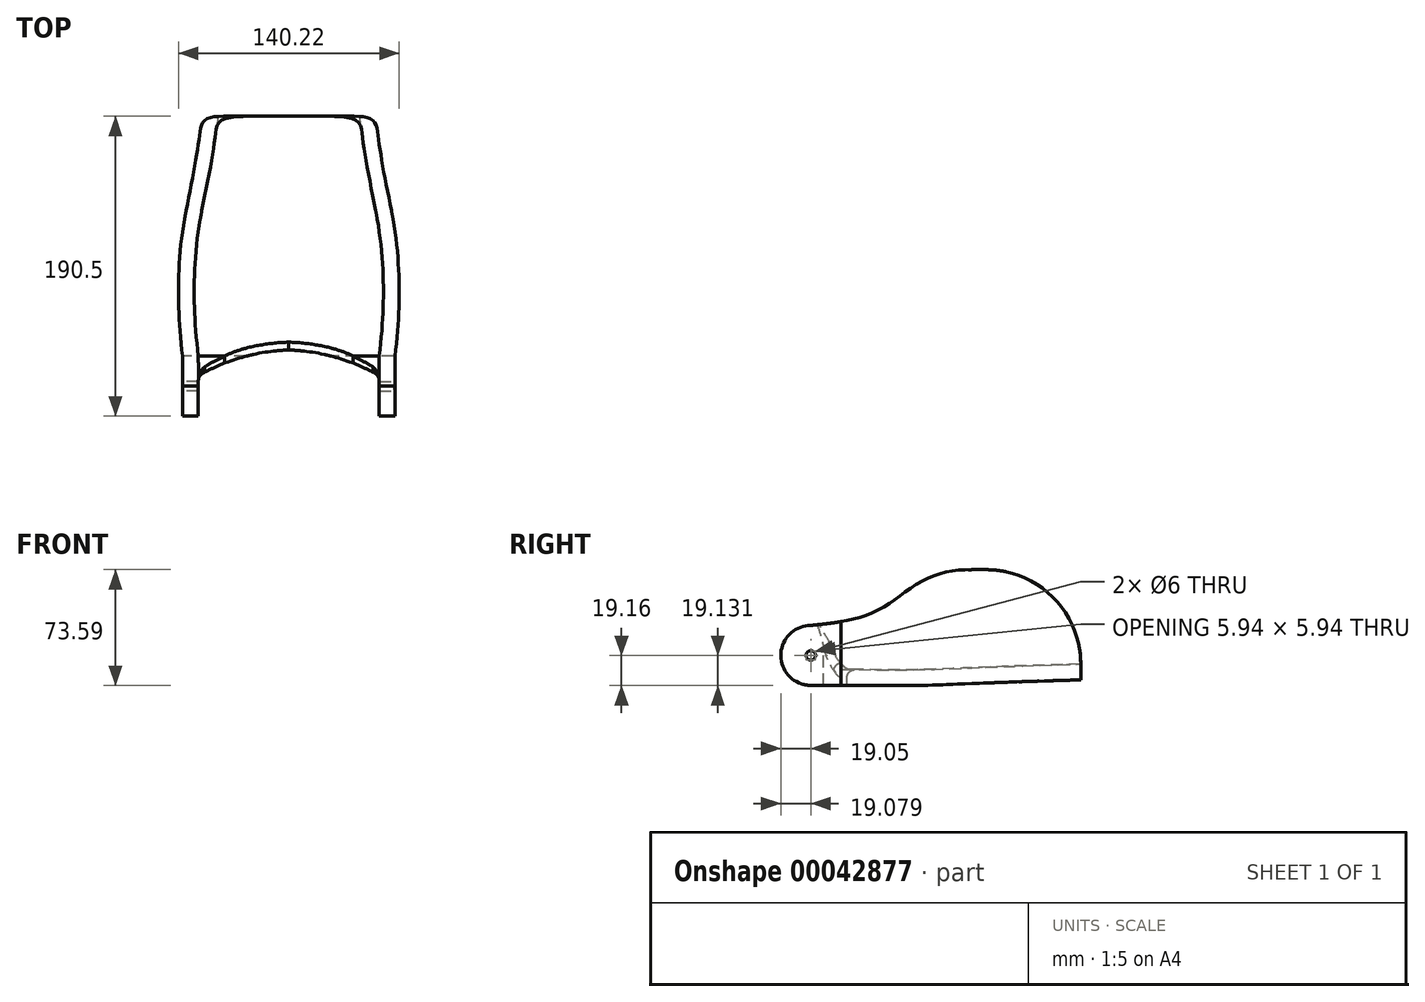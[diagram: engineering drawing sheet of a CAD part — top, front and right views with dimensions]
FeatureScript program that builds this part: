
annotation { "Feature Type Name" : "Feature", "Feature Type Description" : "" }
export const myFeature = defineFeature(function(context is Context, id is Id, definition is map)
    precondition{}
    {
        {
            var Q0;
            Q0=qCreatedBy(makeId("Right.planeOp"),FACE);
            cPlane(context, id + "F0", {"entities" : qUnion([Q0]), "cplaneType" : CPlaneType.OFFSET, "offset" : (115 * mm / 2) + 10 * mm, "width" : 150 * mm, "height" : 150 * mm});
        }
        {
            var Q0;
            Q0=qCreatedBy(makeId("Front.planeOp"),FACE);
            cPlane(context, id + "F1", {"entities" : qUnion([Q0]), "cplaneType" : CPlaneType.OFFSET, "offset" : 114.3 * mm, "width" : 150 * mm, "height" : 150 * mm});
        }
        {
            var Q0;
            Q0=qCreatedBy(makeId("Front.planeOp"),FACE);
            cPlane(context, id + "F2", {"entities" : qUnion([Q0]), "cplaneType" : CPlaneType.OFFSET, "offset" : 76.2 * mm, "width" : 150 * mm, "height" : 150 * mm});
        }
        {
            var Q0;
            Q0=qCreatedBy(makeId("Front.planeOp"),FACE);
            cPlane(context, id + "F3", {"entities" : qUnion([Q0]), "cplaneType" : CPlaneType.OFFSET, "offset" : (76.2 * mm) - 15 * mm, "width" : 150 * mm, "height" : 150 * mm});
        }
        {
            var Q0;
            Q0=qCreatedBy(makeId("Front.planeOp"),FACE);
            cPlane(context, id + "F4", {"entities" : qUnion([Q0]), "cplaneType" : CPlaneType.OFFSET, "offset" : (76.2 * mm) - 49 * mm, "width" : 150 * mm, "height" : 150 * mm});
        }
        {
            var Q0;
            Q0=qCreatedBy(makeId("Top.planeOp"),FACE);
            cPlane(context, id + "F5", {"entities" : qUnion([Q0]), "cplaneType" : CPlaneType.OFFSET, "offset" : 63.5 * mm + 10 * mm, "oppositeDirection" : true, "width" : 150 * mm, "height" : 150 * mm});
        }
        {
            var Q0;
            Q0=qCreatedBy(makeId("Front.planeOp"),FACE);
            cPlane(context, id + "F6", {"entities" : qUnion([Q0]), "cplaneType" : CPlaneType.OFFSET, "offset" : 76.2 * mm, "oppositeDirection" : true, "width" : 150 * mm, "height" : 150 * mm});
        }
        {
            var Q0;
            Q0=qCreatedBy(makeId("Front.planeOp"),FACE);
            cPlane(context, id + "F7", {"entities" : qUnion([Q0]), "cplaneType" : CPlaneType.OFFSET, "offset" : 76.2 * mm - 33.4 * mm, "oppositeDirection" : true, "width" : 150 * mm, "height" : 150 * mm});
        }
        {
            var Q0;
            Q0=qCreatedBy(makeId("Front.planeOp"),FACE);
            cPlane(context, id + "F8", {"entities" : qUnion([Q0]), "cplaneType" : CPlaneType.OFFSET, "offset" : 76.2 * mm - 73.4 * mm, "oppositeDirection" : true, "width" : 150 * mm, "height" : 150 * mm});
        }
        {
            var Q0;
            Q0=qCreatedBy(makeId("Top.planeOp"),FACE);
            var sketch = newSketch(context, id + "F9", { "sketchPlane" : qUnion([Q0])});
            skLineSegment(sketch, "E0", {"start": v(0, 76.2) * mm, "end": v(0, -76.2) * mm, "construction": true});
            skPoint(sketch, "E1", {"position": v(0, 0) * mm});
            skLineSegment(sketch, "E2", {"start": v(0, -76.2) * mm, "end": v(57.5, -76.2) * mm, "construction": true});
            skLineSegment(sketch, "E3", {"start": v(0, -61.2) * mm, "end": v(59, -61.2) * mm, "construction": true});
            skLineSegment(sketch, "E4", {"start": v(0, -27.2) * mm, "end": v(60, -27.2) * mm, "construction": true});
            skLineSegment(sketch, "E5", {"start": v(0, 2.8) * mm, "end": v(57.5, 2.8) * mm, "construction": true});
            skLineSegment(sketch, "E6", {"start": v(0, 42.8) * mm, "end": v(50, 42.8) * mm, "construction": true});
            skLineSegment(sketch, "E7", {"start": v(0, 76.2) * mm, "end": v(45, 76.2) * mm, "construction": true});
            skLineSegment(sketch, "E8.bottom", {"start": v(-157.02, 34.24) * mm, "end": v(-106.22, 34.24) * mm});
            skLineSegment(sketch, "E8.top", {"start": v(-157.02, -16.56) * mm, "end": v(-106.22, -16.56) * mm});
            skLineSegment(sketch, "E8.left", {"start": v(-157.02, 34.24) * mm, "end": v(-157.02, -16.56) * mm});
            skLineSegment(sketch, "E8.right", {"start": v(-106.22, 34.24) * mm, "end": v(-106.22, -16.56) * mm});
            skLineSegment(sketch, "E9", {"start": v(60, 76.2) * mm, "end": v(60, -76.2) * mm, "construction": true});
            skPoint(sketch, "E10", {"position": v(22.5, 76.2) * mm});
            skLineSegment(sketch, "E11", {"start": v(-60, 76.2) * mm, "end": v(-60, -76.2) * mm, "construction": true});
            skLineSegment(sketch, "E12", {"start": v(0, -95.25) * mm, "end": v(57.5, -95.25) * mm, "construction": true});
            skLineSegment(sketch, "E13", {"start": v(0, -114.3) * mm, "end": v(57.5, -114.3) * mm, "construction": true});
            skLineSegment(sketch, "E14", {"start": v(0, -84.2) * mm, "end": v(57.5, -84.2) * mm, "construction": true});
            skPoint(sketch, "E15.visualSharp", {"position": v(57.5, -84.2) * mm});
            skLineSegment(sketch, "E15.filletArc", {"start": v(57.5, -84.2) * mm, "end": v(57.5, -84.2) * mm});
            skLineSegment(sketch, "E16", {"start": v(45, 76.2) * mm, "end": v(55, 76.2) * mm});
            skLineSegment(sketch, "E17", {"start": v(50, 42.8) * mm, "end": v(60, 42.8) * mm, "construction": true});
            skLineSegment(sketch, "E18", {"start": v(57.5, 2.8) * mm, "end": v(67.5, 2.8) * mm, "construction": true});
            skLineSegment(sketch, "E19", {"start": v(60, -27.2) * mm, "end": v(70, -27.2) * mm, "construction": true});
            skLineSegment(sketch, "E20", {"start": v(59, -61.2) * mm, "end": v(69, -61.2) * mm, "construction": true});
            skLineSegment(sketch, "E21", {"start": v(57.5, -76.2) * mm, "end": v(67.5, -76.2) * mm, "construction": true});
            skLineSegment(sketch, "E22", {"start": v(57.5, -84.2) * mm, "end": v(67.5, -84.2) * mm});
            skLineSegment(sketch, "E23", {"start": v(57.5, -95.25) * mm, "end": v(67.5, -95.25) * mm});
            skLineSegment(sketch, "E24", {"start": v(57.5, -114.3) * mm, "end": v(67.5, -114.3) * mm});
            skFitSpline(sketch, "E25", {"points": [v(55, 76.2) * mm, v(60, 42.8) * mm, v(67.5, 2.8) * mm, v(70, -27.2) * mm, v(69, -61.2) * mm, v(67.5, -76.2) * mm, v(67.5, -84.2) * mm, v(67.5, -95.25) * mm, v(67.5, -114.3) * mm], "startDerivative": vector(28.82, -213.97) * mm, "endDerivative": vector(-0.1, -161.58) * mm});
            skLineSegment(sketch, "E26", {"start": v(60, -76.2) * mm, "end": v(60, -137.07) * mm, "construction": true});
            skFitSpline(sketch, "E27", {"points": [v(45, 76.2) * mm, v(50, 42.8) * mm, v(57.5, 2.8) * mm, v(60, -27.2) * mm, v(59, -61.2) * mm, v(57.5, -76.2) * mm, v(57.5, -84.2) * mm, v(57.5, -95.25) * mm, v(57.5, -114.3) * mm], "startDerivative": vector(29.26, -219.54) * mm, "endDerivative": vector(0.26, -174.77) * mm});
            skLineSegment(sketch, "E28", {"start": v(0, -114.05) * mm, "end": v(57.5, -114.05) * mm, "construction": true});
            skLineSegment(sketch, "E29", {"start": v(57.5, -114.05) * mm, "end": v(67.5, -114.05) * mm});
            skSolve(sketch);
        }
        {
            var Q0;
            Q0=qCreatedBy(id+"F1.planeOp",FACE);
            var sketch = newSketch(context, id + "F10", { "sketchPlane" : qUnion([Q0])});
            skLineSegment(sketch, "E30", {"start": v(0, 0) * mm, "end": v(57.5, 0) * mm, "construction": true});
            skLineSegment(sketch, "E31", {"start": v(57.5, 0) * mm, "end": v(67.5, 0) * mm});
            skLineSegment(sketch, "E32", {"start": v(0, 0) * mm, "end": v(0, -63.5) * mm, "construction": true});
            skLineSegment(sketch, "E33", {"start": v(0, 0) * mm, "end": v(52.5, 0) * mm, "construction": true});
            skLineSegment(sketch, "E34", {"start": v(57.5, 0) * mm, "end": v(57.5, -31.5) * mm});
            skLineSegment(sketch, "E35", {"start": v(25.5, -63.5) * mm, "end": v(0, -63.5) * mm});
            skLineSegment(sketch, "E36", {"start": v(0, -63.5) * mm, "end": v(0, -73.5) * mm});
            skArc(sketch, "E37.filletArc", {"start": v(25.5, -63.5) * mm, "mid": v(48.13, -54.13) * mm, "end": v(57.5, -31.5) * mm});
            skPoint(sketch, "E38", {"position": v(0, -35.5) * mm});
            skLineSegment(sketch, "E39", {"start": v(0, -35.5) * mm, "end": v(67.5, -35.5) * mm, "construction": true});
            skLineSegment(sketch, "E40", {"start": v(67.5, 0) * mm, "end": v(67.5, -72.5) * mm});
            skLineSegment(sketch, "E41", {"start": v(66.5, -73.5) * mm, "end": v(0, -73.5) * mm});
            skPoint(sketch, "E42.visualSharp", {"position": v(67.5, -73.5) * mm});
            skArc(sketch, "E42.filletArc", {"start": v(66.5, -73.5) * mm, "mid": v(67.2, -73.2) * mm, "end": v(67.5, -72.5) * mm});
            skSolve(sketch);
        }
        {
            var Q0;
            Q0=qCreatedBy(id+"F2.planeOp",FACE);
            var sketch = newSketch(context, id + "F11", { "sketchPlane" : qUnion([Q0])});
            skLineSegment(sketch, "E43", {"start": v(0, 0) * mm, "end": v(57.5, 0) * mm, "construction": true});
            skLineSegment(sketch, "E44", {"start": v(0, 0) * mm, "end": v(0, -63.5) * mm, "construction": true});
            skLineSegment(sketch, "E45", {"start": v(57.5, 0) * mm, "end": v(67.5, 0) * mm});
            skLineSegment(sketch, "E46", {"start": v(0, -63.5) * mm, "end": v(0, -73.5) * mm});
            skLineSegment(sketch, "E47", {"start": v(57.5, 0) * mm, "end": v(57.5, -31.5) * mm});
            skLineSegment(sketch, "E48", {"start": v(25.5, -63.5) * mm, "end": v(0, -63.5) * mm});
            skLineSegment(sketch, "E49", {"start": v(67.5, -72.5) * mm, "end": v(67.5, 0) * mm});
            skPoint(sketch, "E50.visualSharp", {"position": v(57.5, -63.5) * mm});
            skArc(sketch, "E50.filletArc", {"start": v(25.5, -63.5) * mm, "mid": v(48.13, -54.13) * mm, "end": v(57.5, -31.5) * mm});
            skLineSegment(sketch, "E51", {"start": v(66.5, -73.5) * mm, "end": v(0, -73.5) * mm});
            skPoint(sketch, "E52.visualSharp", {"position": v(67.5, -73.5) * mm});
            skArc(sketch, "E52.filletArc", {"start": v(66.5, -73.5) * mm, "mid": v(67.2, -73.2) * mm, "end": v(67.5, -72.5) * mm});
            skSolve(sketch);
        }
        {
            var Q0;
            Q0=qCreatedBy(id+"F3.planeOp",FACE);
            var sketch = newSketch(context, id + "F12", { "sketchPlane" : qUnion([Q0])});
            skLineSegment(sketch, "E53", {"start": v(0, 0) * mm, "end": v(59, 0) * mm, "construction": true});
            skLineSegment(sketch, "E54", {"start": v(0, 0) * mm, "end": v(0, -63.5) * mm, "construction": true});
            skLineSegment(sketch, "E55", {"start": v(59, 0) * mm, "end": v(69, 0) * mm});
            skLineSegment(sketch, "E56", {"start": v(0, -63.5) * mm, "end": v(0, -73.5) * mm});
            skLineSegment(sketch, "E57", {"start": v(59, 0) * mm, "end": v(59, -31.5) * mm});
            skLineSegment(sketch, "E58", {"start": v(27, -63.5) * mm, "end": v(0, -63.5) * mm});
            skLineSegment(sketch, "E59", {"start": v(69, 0) * mm, "end": v(69, -63.5) * mm});
            skLineSegment(sketch, "E60", {"start": v(59, -73.5) * mm, "end": v(0, -73.5) * mm});
            skPoint(sketch, "E61.visualSharp", {"position": v(59, -63.5) * mm});
            skArc(sketch, "E61.filletArc", {"start": v(27, -63.5) * mm, "mid": v(49.63, -54.13) * mm, "end": v(59, -31.5) * mm});
            skPoint(sketch, "E62.visualSharp", {"position": v(69, -73.5) * mm});
            skArc(sketch, "E62.filletArc", {"start": v(59, -73.5) * mm, "mid": v(66.07, -70.57) * mm, "end": v(69, -63.5) * mm});
            skSolve(sketch);
        }
        {
            var Q0;
            Q0=qCreatedBy(id+"F4.planeOp",FACE);
            var sketch = newSketch(context, id + "F13", { "sketchPlane" : qUnion([Q0])});
            skLineSegment(sketch, "E63", {"start": v(0, 0) * mm, "end": v(60, 0) * mm, "construction": true});
            skLineSegment(sketch, "E64", {"start": v(0, 0) * mm, "end": v(0, -63.5) * mm, "construction": true});
            skLineSegment(sketch, "E65", {"start": v(60, 0) * mm, "end": v(70, 0) * mm});
            skLineSegment(sketch, "E66", {"start": v(0, -63.5) * mm, "end": v(0, -73.5) * mm});
            skLineSegment(sketch, "E67", {"start": v(60, 0) * mm, "end": v(60, -31.5) * mm});
            skLineSegment(sketch, "E68", {"start": v(28, -63.5) * mm, "end": v(0, -63.5) * mm});
            skLineSegment(sketch, "E69", {"start": v(70, 0) * mm, "end": v(70, -45.5) * mm});
            skLineSegment(sketch, "E70", {"start": v(42, -73.5) * mm, "end": v(0, -73.5) * mm});
            skPoint(sketch, "E71.visualSharp", {"position": v(60, -63.5) * mm});
            skArc(sketch, "E71.filletArc", {"start": v(28, -63.5) * mm, "mid": v(50.63, -54.13) * mm, "end": v(60, -31.5) * mm});
            skPoint(sketch, "E72.visualSharp", {"position": v(70, -73.5) * mm});
            skArc(sketch, "E72.filletArc", {"start": v(42, -73.5) * mm, "mid": v(61.8, -65.3) * mm, "end": v(70, -45.5) * mm});
            skSolve(sketch);
        }
        {
            var Q0;
            Q0=qCreatedBy(id+"F6.planeOp",FACE);
            var sketch = newSketch(context, id + "F14", { "sketchPlane" : qUnion([Q0])});
            skLineSegment(sketch, "E73", {"start": v(0, 0) * mm, "end": v(0, -60) * mm, "construction": true});
            skLineSegment(sketch, "E74", {"start": v(0, 0) * mm, "end": v(45, 0) * mm, "construction": true});
            skLineSegment(sketch, "E75", {"start": v(0, -60) * mm, "end": v(15, -60) * mm});
            skLineSegment(sketch, "E76", {"start": v(45, 0) * mm, "end": v(55, 0) * mm});
            skLineSegment(sketch, "E77", {"start": v(0, -60) * mm, "end": v(0, -70) * mm});
            skLineSegment(sketch, "E78", {"start": v(0, -70) * mm, "end": v(15, -70) * mm});
            skLineSegment(sketch, "E79", {"start": v(55, -30) * mm, "end": v(55, 0) * mm});
            skLineSegment(sketch, "E80", {"start": v(45, -30) * mm, "end": v(45, 0) * mm});
            skPoint(sketch, "E81.visualSharp", {"position": v(45, -60) * mm});
            skArc(sketch, "E81.filletArc", {"start": v(15, -60) * mm, "mid": v(36.21, -51.21) * mm, "end": v(45, -30) * mm});
            skPoint(sketch, "E82.visualSharp", {"position": v(55, -70) * mm});
            skArc(sketch, "E82.filletArc", {"start": v(15, -70) * mm, "mid": v(43.28, -58.28) * mm, "end": v(55, -30) * mm});
            skSolve(sketch);
        }
        {
            var Q0;
            Q0=qCreatedBy(id+"F7.planeOp",FACE);
            var sketch = newSketch(context, id + "F15", { "sketchPlane" : qUnion([Q0])});
            skLineSegment(sketch, "E83", {"start": v(0, 0) * mm, "end": v(50, 0) * mm, "construction": true});
            skLineSegment(sketch, "E84", {"start": v(0, 0) * mm, "end": v(0, -61) * mm, "construction": true});
            skLineSegment(sketch, "E85", {"start": v(50, 0) * mm, "end": v(60, 0) * mm});
            skLineSegment(sketch, "E86", {"start": v(0, -61) * mm, "end": v(0, -71) * mm});
            skLineSegment(sketch, "E87", {"start": v(50, 0) * mm, "end": v(50, -31) * mm});
            skLineSegment(sketch, "E88", {"start": v(20, -61) * mm, "end": v(0, -61) * mm});
            skLineSegment(sketch, "E89", {"start": v(60, 0) * mm, "end": v(60, -31) * mm});
            skLineSegment(sketch, "E90", {"start": v(20, -71) * mm, "end": v(0, -71) * mm});
            skPoint(sketch, "E91.visualSharp", {"position": v(50, -61) * mm});
            skArc(sketch, "E91.filletArc", {"start": v(20, -61) * mm, "mid": v(41.21, -52.21) * mm, "end": v(50, -31) * mm});
            skPoint(sketch, "E92.visualSharp", {"position": v(60, -71) * mm});
            skArc(sketch, "E92.filletArc", {"start": v(20, -71) * mm, "mid": v(48.28, -59.28) * mm, "end": v(60, -31) * mm});
            skSolve(sketch);
        }
        {
            var Q0;
            Q0=qCreatedBy(id+"F8.planeOp",FACE);
            var sketch = newSketch(context, id + "F16", { "sketchPlane" : qUnion([Q0])});
            skLineSegment(sketch, "E93", {"start": v(0, 0) * mm, "end": v(57.5, 0) * mm, "construction": true});
            skLineSegment(sketch, "E94", {"start": v(0, 0) * mm, "end": v(0, -62.5) * mm, "construction": true});
            skLineSegment(sketch, "E95", {"start": v(57.5, 0) * mm, "end": v(67.5, 0) * mm});
            skLineSegment(sketch, "E96", {"start": v(0, -62.5) * mm, "end": v(0, -72.5) * mm});
            skLineSegment(sketch, "E97", {"start": v(57.5, 0) * mm, "end": v(57.5, -31.5) * mm});
            skLineSegment(sketch, "E98", {"start": v(26.5, -62.5) * mm, "end": v(0, -62.5) * mm});
            skLineSegment(sketch, "E99", {"start": v(67.5, 0) * mm, "end": v(67.5, -31.5) * mm});
            skLineSegment(sketch, "E100", {"start": v(26.5, -72.5) * mm, "end": v(0, -72.5) * mm});
            skPoint(sketch, "E101.visualSharp", {"position": v(57.5, -62.5) * mm});
            skArc(sketch, "E101.filletArc", {"start": v(26.5, -62.5) * mm, "mid": v(48.42, -53.42) * mm, "end": v(57.5, -31.5) * mm});
            skPoint(sketch, "E102.visualSharp", {"position": v(67.5, -72.5) * mm});
            skArc(sketch, "E102.filletArc", {"start": v(26.5, -72.5) * mm, "mid": v(55.5, -60.5) * mm, "end": v(67.5, -31.5) * mm});
            skSolve(sketch);
        }
        {
            var Q0;
            Q0=qCreatedBy(makeId("Right.planeOp"),FACE);
            var sketch = newSketch(context, id + "F17", { "sketchPlane" : qUnion([Q0])});
            skLineSegment(sketch, "E103", {"start": v(-76.2, 0) * mm, "end": v(76.2, 0) * mm, "construction": true});
            skLineSegment(sketch, "E104", {"start": v(76.2, 0) * mm, "end": v(76.2, -60) * mm, "construction": true});
            skLineSegment(sketch, "E105", {"start": v(42.8, 0) * mm, "end": v(42.8, -61) * mm, "construction": true});
            skLineSegment(sketch, "E106", {"start": v(2.8, 0) * mm, "end": v(2.8, -62.5) * mm, "construction": true});
            skLineSegment(sketch, "E107", {"start": v(-27.2, 0) * mm, "end": v(-27.2, -63.5) * mm, "construction": true});
            skLineSegment(sketch, "E108", {"start": v(-61.2, 0) * mm, "end": v(-61.2, -63.5) * mm, "construction": true});
            skLineSegment(sketch, "E109", {"start": v(-76.2, 0) * mm, "end": v(-76.2, -63.5) * mm, "construction": true});
            skPoint(sketch, "E110", {"position": v(0, 0) * mm});
            skLineSegment(sketch, "E111", {"start": v(76.2, -60) * mm, "end": v(76.2, -70) * mm});
            skLineSegment(sketch, "E112", {"start": v(42.8, -61) * mm, "end": v(42.8, -71) * mm});
            skLineSegment(sketch, "E113", {"start": v(2.8, -62.5) * mm, "end": v(2.8, -72.5) * mm});
            skLineSegment(sketch, "E114", {"start": v(-27.2, -63.5) * mm, "end": v(-27.2, -73.5) * mm});
            skLineSegment(sketch, "E115", {"start": v(-61.2, -63.5) * mm, "end": v(-61.2, -73.5) * mm});
            skLineSegment(sketch, "E116", {"start": v(-76.2, -63.5) * mm, "end": v(-76.2, -73.5) * mm});
            skLineSegment(sketch, "E117", {"start": v(-84.2, 0) * mm, "end": v(-84.2, -63.5) * mm, "construction": true});
            skLineSegment(sketch, "E118", {"start": v(-84.2, -63.5) * mm, "end": v(-84.2, -73.5) * mm});
            skLineSegment(sketch, "E119", {"start": v(-95.25, 0) * mm, "end": v(-95.25, -63.5) * mm, "construction": true});
            skLineSegment(sketch, "E120", {"start": v(-114.3, 0) * mm, "end": v(-114.3, -63.5) * mm, "construction": true});
            skLineSegment(sketch, "E121", {"start": v(-95.25, -63.5) * mm, "end": v(-95.25, -73.5) * mm});
            skLineSegment(sketch, "E122", {"start": v(-114.3, -63.5) * mm, "end": v(-114.3, -73.5) * mm});
            skFitSpline(sketch, "E123", {"points": [v(76.2, -60) * mm, v(42.8, -61) * mm, v(2.8, -62.5) * mm, v(-27.2, -63.5) * mm, v(-61.2, -63.5) * mm, v(-76.2, -63.5) * mm, v(-84.2, -63.5) * mm, v(-95.25, -63.5) * mm, v(-114.3, -63.5) * mm], "startDerivative": vector(-217.44, -6.1) * mm, "endDerivative": vector(-173.87, 0) * mm});
            skFitSpline(sketch, "E124", {"points": [v(76.2, -70) * mm, v(42.8, -71) * mm, v(2.8, -72.5) * mm, v(-27.2, -73.5) * mm, v(-61.2, -73.5) * mm, v(-76.2, -73.5) * mm, v(-84.2, -73.5) * mm, v(-95.25, -73.5) * mm, v(-114.3, -73.5) * mm], "startDerivative": vector(-217.36, -6.1) * mm, "endDerivative": vector(-173.09, 0) * mm});
            skLineSegment(sketch, "E125.bottom", {"start": v(-173.81, 0) * mm, "end": v(-223.81, 0) * mm, "construction": true});
            skLineSegment(sketch, "E125.top", {"start": v(-173.81, -50) * mm, "end": v(-223.81, -50) * mm, "construction": true});
            skLineSegment(sketch, "E125.left", {"start": v(-173.81, 0) * mm, "end": v(-173.81, -50) * mm, "construction": true});
            skLineSegment(sketch, "E125.right", {"start": v(-223.81, 0) * mm, "end": v(-223.81, -50) * mm, "construction": true});
            skSolve(sketch);
        }
        {
            var Q0;
            Q0=makeQuery(id+"F14.imprint","IMPRINT",FACE,{"disambiguationData":[TD([[makeQuery(id+"F14.imprint","IMPRINT",EDGE,{"derivedFrom":sQuery(id+"F14.wireOp",EDGE,"E75")}),-1.0]])]});
            var Q1;
            Q1=makeQuery(id+"F15.imprint","IMPRINT",FACE,{"disambiguationData":[TD([[makeQuery(id+"F15.imprint","IMPRINT",EDGE,{"derivedFrom":sQuery(id+"F15.wireOp",EDGE,"E85")}),-1.0]])]});
            var Q2;
            Q2=makeQuery(id+"F16.imprint","IMPRINT",FACE,{"disambiguationData":[TD([[makeQuery(id+"F16.imprint","IMPRINT",EDGE,{"derivedFrom":sQuery(id+"F16.wireOp",EDGE,"E95")}),-1.0]])]});
            var Q3;
            Q3=makeQuery(id+"F13.imprint","IMPRINT",FACE,{"disambiguationData":[TD([[makeQuery(id+"F13.imprint","IMPRINT",EDGE,{"derivedFrom":sQuery(id+"F13.wireOp",EDGE,"E65")}),-1.0]])]});
            var Q4;
            Q4=makeQuery(id+"F12.imprint","IMPRINT",FACE,{"disambiguationData":[TD([[makeQuery(id+"F12.imprint","IMPRINT",EDGE,{"derivedFrom":sQuery(id+"F12.wireOp",EDGE,"E55")}),-1.0]])]});
            var Q5;
            Q5=makeQuery(id+"F11.imprint","IMPRINT",FACE,{"disambiguationData":[TD([[makeQuery(id+"F11.imprint","IMPRINT",EDGE,{"derivedFrom":sQuery(id+"F11.wireOp",EDGE,"E45")}),-1.0]])]});
            loft(context, id + "F18", {"sheetProfilesArray" : [{ "sheetProfileEntities" : qUnion([Q0]) }, { "sheetProfileEntities" : qUnion([Q1]) }, { "sheetProfileEntities" : qUnion([Q2]) }, { "sheetProfileEntities" : qUnion([Q3]) }, { "sheetProfileEntities" : qUnion([Q4]) }, { "sheetProfileEntities" : qUnion([Q5]) }]});
        }
        {
            var Q1;
            Q1=makeQuery(id+"F11.imprint","IMPRINT",FACE,{"disambiguationData":[TD([[makeQuery(id+"F11.imprint","IMPRINT",EDGE,{"derivedFrom":sQuery(id+"F11.wireOp",EDGE,"E45")}),-1.0]])]});
            var Q2;
            Q2=makeQuery(id+"F10.imprint","IMPRINT",FACE,{"disambiguationData":[TD([[makeQuery(id+"F10.imprint","IMPRINT",EDGE,{"derivedFrom":sQuery(id+"F10.wireOp",EDGE,"E31")}),-1.0]])]});
            loft(context, id + "F19", {"operationType" : NewBodyOperationType.ADD, "sheetProfilesArray" : [{ "sheetProfileEntities" : qUnion([Q1]) }, { "sheetProfileEntities" : qUnion([Q2]) }]});
        }
        {
            var Q0;
            Q0=makeQuery(id+"F18.opLoft","MID_CAP_EDGE",EDGE,{"disambiguationData":[OSD([sQuery(id+"F14.wireOp",EDGE,"E76"),sQuery(id+"F14.wireOp",EDGE,"E79"),sQuery(id+"F14.wireOp",EDGE,"E80")])],"capPos":0.0});
            fillet(context, id + "F20", {"entities" : qUnion([Q0]), "radius" : 60 * mm, "tangentPropagation" : true, "allowEdgeOverflow" : false});
        }
        {
            var Q0;
            Q0=qCreatedBy(id+"F0.planeOp",FACE);
            var sketch = newSketch(context, id + "F21", { "sketchPlane" : qUnion([Q0])});
            skCircle(sketch, "E126", {"center": v(-95.25, -54.43) * mm, "radius": 19.05 * mm});
            skLineSegment(sketch, "E127", {"start": v(-76.2, 0) * mm, "end": v(76.2, 0) * mm, "construction": true});
            skLineSegment(sketch, "E128", {"start": v(-76.2, 0) * mm, "end": v(-76.2, -63.48) * mm, "construction": true});
            skLineSegment(sketch, "E129", {"start": v(-76.2, -63.48) * mm, "end": v(-76.2, -73.48) * mm, "construction": true});
            skLineSegment(sketch, "E130", {"start": v(-76.2, -73.48) * mm, "end": v(-114.3, -73.48) * mm, "construction": true});
            skLineSegment(sketch, "E131", {"start": v(-76.2, -35.38) * mm, "end": v(-114.3, -35.38) * mm, "construction": true});
            skLineSegment(sketch, "E132", {"start": v(-76.2, 0) * mm, "end": v(-114.3, 0) * mm, "construction": true});
            skLineSegment(sketch, "E133", {"start": v(-95.25, -54.43) * mm, "end": v(-114.3, -54.43) * mm, "construction": true});
            skLineSegment(sketch, "E134", {"start": v(-95.25, -54.43) * mm, "end": v(-95.25, -73.48) * mm, "construction": true});
            skLineSegment(sketch, "E135", {"start": v(-114.3, -54.43) * mm, "end": v(-114.3, -73.48) * mm});
            skLineSegment(sketch, "E136", {"start": v(-95.25, -73.48) * mm, "end": v(-114.3, -73.48) * mm});
            skLineSegment(sketch, "E137", {"start": v(-127.04, -54.43) * mm, "end": v(-127.04, -88.5) * mm});
            skLineSegment(sketch, "E138", {"start": v(-127.04, -88.5) * mm, "end": v(-95.25, -88.5) * mm});
            skLineSegment(sketch, "E139", {"start": v(-95.25, -88.5) * mm, "end": v(-95.25, -73.48) * mm});
            skLineSegment(sketch, "E140", {"start": v(-127.04, -54.43) * mm, "end": v(-127.04, 0) * mm});
            skLineSegment(sketch, "E141", {"start": v(-127.04, 0) * mm, "end": v(0, 0) * mm, "construction": true});
            skLineSegment(sketch, "E142", {"start": v(-51.2, 0) * mm, "end": v(-51.2, -25) * mm, "construction": true});
            skPoint(sketch, "E143", {"position": v(-76.2, -33) * mm});
            skLineSegment(sketch, "E144", {"start": v(-29.2, 0) * mm, "end": v(-29.2, -10) * mm, "construction": true});
            skLineSegment(sketch, "E145", {"start": v(-9.2, 0) * mm, "end": v(-9.2, -1.5) * mm, "construction": true});
            skPoint(sketch, "E146", {"position": v(10.8, 0) * mm});
            skFitSpline(sketch, "E147", {"points": [v(-95.25, -35.38) * mm, v(-76.2, -33) * mm, v(-51.2, -25) * mm, v(-29.2, -10) * mm, v(-9.2, -1.5) * mm, v(10.8, 0) * mm], "startDerivative": vector(95.45, 9) * mm, "endDerivative": vector(138.5, 0) * mm});
            skLineSegment(sketch, "E148", {"start": v(-127.04, 0) * mm, "end": v(-127.04, 22.7) * mm});
            skLineSegment(sketch, "E149", {"start": v(-127.04, 22.7) * mm, "end": v(10.8, 22.7) * mm});
            skLineSegment(sketch, "E150", {"start": v(10.8, 22.7) * mm, "end": v(10.8, 0) * mm});
            skCircle(sketch, "E151", {"center": v(-95.25, -54.43) * mm, "radius": 3 * mm});
            skSolve(sketch);
        }
        {
            var Q0;
            {var subQ1=sQuery(id+"F21.wireOp",EDGE,"E135");Q0=makeQuery(id+"F21.imprint","IMPRINT",FACE,{"disambiguationData":[TD([[makeQuery(id+"F21.imprint","IMPRINT",EDGE,{"derivedFrom":subQ1}),-1.0]])]});}
            var Q1;
            {var subQ0=sQuery(id+"F21.wireOp",EDGE,"E135");Q1=makeQuery(id+"F21.imprint","IMPRINT",FACE,{"disambiguationData":[TD([[makeQuery(id+"F21.imprint","IMPRINT",EDGE,{"derivedFrom":subQ0}),1.0]])]});}
            extrude(context, id + "F22", {"entities" : qUnion([Q0, Q1]), "operationType" : NewBodyOperationType.REMOVE, "endBound" : BoundingType.SYMMETRIC, "oppositeDirection" : true, "depth" : 140 * mm});
        }
        {
            var Q0;
            Q0=makeQuery(id+"F21.imprint","IMPRINT",FACE,{"disambiguationData":[TD([[makeQuery(id+"F21.imprint","IMPRINT",EDGE,{"derivedFrom":sQuery(id+"F21.wireOp",EDGE,"E151")}),1.0]])]});
            extrude(context, id + "F23", {"entities" : qUnion([Q0]), "operationType" : NewBodyOperationType.REMOVE, "endBound" : BoundingType.THROUGH_ALL, "oppositeDirection" : true, "depth" : 25 * mm});
        }
        {
            var Q0;
            Q0=qCreatedBy(id+"F5.planeOp",FACE);
            var sketch = newSketch(context, id + "F24", { "sketchPlane" : qUnion([Q0])});
            skLineSegment(sketch, "E152", {"start": v(0, 76.2) * mm, "end": v(0, -76.2) * mm});
            skLineSegment(sketch, "E153", {"start": v(0, -114.3) * mm, "end": v(57.5, -114.3) * mm});
            skLineSegment(sketch, "E154", {"start": v(0, -76.2) * mm, "end": v(0, -114.3) * mm, "construction": true});
            skLineSegment(sketch, "E155", {"start": v(0, -95.25) * mm, "end": v(57.5, -95.25) * mm, "construction": true});
            skLineSegment(sketch, "E156.rect.bottom", {"start": v(67.5, -98.25) * mm, "end": v(57.5, -98.25) * mm, "construction": true});
            skLineSegment(sketch, "E156.rect.top", {"start": v(67.5, -92.25) * mm, "end": v(57.5, -92.25) * mm, "construction": true});
            skLineSegment(sketch, "E156.rect.left", {"start": v(67.5, -98.25) * mm, "end": v(67.5, -92.25) * mm, "construction": true});
            skLineSegment(sketch, "E156.rect.right", {"start": v(57.5, -98.25) * mm, "end": v(57.5, -92.25) * mm, "construction": true});
            skPoint(sketch, "E156.rect.middle", {"position": v(62.5, -95.25) * mm});
            skCircle(sketch, "E157", {"center": v(51, -92.25) * mm, "radius": 6.5 * mm});
            skLineSegment(sketch, "E158", {"start": v(57.5, -95.25) * mm, "end": v(57.5, -92.25) * mm, "construction": true});
            skLineSegment(sketch, "E159", {"start": v(0, -72.2) * mm, "end": v(-24.84, -72.2) * mm, "construction": true});
            skCircle(sketch, "E160", {"center": v(-4.1, -196.33) * mm, "radius": 124.13 * mm});
            skPoint(sketch, "E160.first.point", {"position": v(52.79, -86) * mm});
            skPoint(sketch, "E160.second.point", {"position": v(27.16, -76.2) * mm});
            skPoint(sketch, "E160.third.point", {"position": v(-22.84, -73.62) * mm});
            skLineSegment(sketch, "E161", {"start": v(0, -72.2) * mm, "end": v(0, -114.3) * mm});
            skLineSegment(sketch, "E162", {"start": v(57.5, -114.3) * mm, "end": v(57.5, -92.25) * mm});
            skSolve(sketch);
        }
        {
            var Q0;
            {var subQ7=sQuery(id+"F24.wireOp",EDGE,"E153");Q0=makeQuery(id+"F24.imprint","IMPRINT",FACE,{"disambiguationData":[TD([[makeQuery(id+"F24.imprint","IMPRINT",EDGE,{"derivedFrom":subQ7}),1.0]])]});}
            var Q1;
            {var subQ0=sQuery(id+"F24.wireOp",EDGE,"E157");var subQ1=makeQuery(id+"F24.imprint","INTERSECT",VERTEX,{"derivedFrom":[subQ0,sQuery(id+"F24.wireOp",EDGE,"E162")]});Q1=makeQuery(id+"F24.imprint","IMPRINT",FACE,{"disambiguationData":[TD([[makeQuery(id+"F24.imprint","IMPRINT",EDGE,{"disambiguationData":[TD([[subQ1,-1.0]])],"derivedFrom":subQ0}),1.0]])]});}
            var Q2;
            {var subQ3=sQuery(id+"F24.wireOp",EDGE,"E161");var subQ6=makeQuery(id+"F24.imprint","IMPRINT",VERTEX,{"derivedFrom":subQ3});Q2=makeQuery(id+"F24.imprint","IMPRINT",FACE,{"disambiguationData":[TD([[makeQuery(id+"F24.imprint","IMPRINT",EDGE,{"disambiguationData":[TD([[subQ6,1.0]])],"derivedFrom":subQ3}),1.0]])]});}
            var Q3;
            {var subQ0=sQuery(id+"F24.wireOp",EDGE,"E161");var subQ1=sQuery(id+"F24.wireOp",EDGE,"4ed179fe-1dec-4f78-bcb3-8e963e810ee6");var subQ2=makeQuery(id+"F24.imprint","INTERSECT",VERTEX,{"disambiguationData":[OD(0.0)],"derivedFrom":[subQ1,subQ0]});Q3=makeQuery(id+"F24.imprint","IMPRINT",FACE,{"disambiguationData":[TD([[makeQuery(id+"F24.imprint","IMPRINT",EDGE,{"disambiguationData":[TD([[subQ2,1.0]])],"derivedFrom":subQ1}),1.0]])]});}
            extrude(context, id + "F25", {"entities" : qUnion([Q0, Q1, Q2, Q3]), "operationType" : NewBodyOperationType.REMOVE, "endBound" : BoundingType.SYMMETRIC, "oppositeDirection" : true, "depth" : 101.6 * mm});
        }
        {
            var Q0;
            Q0=makeQuery(id+"F25.boolean.opBoolean","INTERSECT",EDGE,{"derivedFrom":[makeQuery(id+"F18.opLoft","SWEPT_FACE",FACE,{"disambiguationData":[OSD([sQuery(id+"F14.wireOp",EDGE,"E76"),sQuery(id+"F14.wireOp",EDGE,"E80"),sQuery(id+"F14.wireOp",EDGE,"E81.filletArc"),sQuery(id+"F15.wireOp",EDGE,"E85"),sQuery(id+"F15.wireOp",EDGE,"E87"),sQuery(id+"F15.wireOp",EDGE,"E91.filletArc")])]}),makeQuery(id+"F25.opExtrude","SWEPT_FACE",FACE,{"disambiguationData":[OSD([sQuery(id+"F24.wireOp",EDGE,"E160")])]})]});
            var Q1;
            Q1=makeQuery(id+"F25.boolean.opBoolean","INTERSECT",EDGE,{"derivedFrom":[makeQuery(id+"F19.opLoft","SWEPT_FACE",FACE,{"disambiguationData":[OSD([sQuery(id+"F10.wireOp",EDGE,"E34"),sQuery(id+"F10.wireOp",EDGE,"E35"),sQuery(id+"F10.wireOp",EDGE,"E37.filletArc"),sQuery(id+"F11.wireOp",EDGE,"E47"),sQuery(id+"F11.wireOp",EDGE,"E48"),sQuery(id+"F11.wireOp",EDGE,"E50.filletArc")])]}),makeQuery(id+"F25.opExtrude","SWEPT_FACE",FACE,{"disambiguationData":[OSD([sQuery(id+"F24.wireOp",EDGE,"E160")])]})]});
            var Q2;
            Q2=makeQuery(id+"F25.boolean.opBoolean","INTERSECT",EDGE,{"derivedFrom":[makeQuery(id+"F19.opLoft","SWEPT_FACE",FACE,{"disambiguationData":[OSD([sQuery(id+"F10.wireOp",EDGE,"E34"),sQuery(id+"F10.wireOp",EDGE,"E35"),sQuery(id+"F10.wireOp",EDGE,"E37.filletArc"),sQuery(id+"F11.wireOp",EDGE,"E47"),sQuery(id+"F11.wireOp",EDGE,"E48"),sQuery(id+"F11.wireOp",EDGE,"E50.filletArc")])]}),makeQuery(id+"F25.opExtrude","SWEPT_FACE",FACE,{"disambiguationData":[OSD([sQuery(id+"F24.wireOp",EDGE,"E157")])]})]});
            fillet(context, id + "F26", {"entities" : qUnion([Q0, Q1, Q2]), "radius" : 5 * mm, "tangentPropagation" : true, "allowEdgeOverflow" : false});
        }
        {
            var Q0;
            Q0=makeQuery(id+"F18.opLoft","SWEPT_BODY",BODY,{"disambiguationData":[OSD([makeQuery(id+"F11.imprint","IMPRINT",FACE,{"disambiguationData":[TD([[makeQuery(id+"F11.imprint","IMPRINT",EDGE,{"derivedFrom":sQuery(id+"F11.wireOp",EDGE,"E45")}),-1.0]])]}),sQuery(id+"F12.wireOp",EDGE,"E55"),sQuery(id+"F13.wireOp",EDGE,"E65"),makeQuery(id+"F14.imprint","IMPRINT",FACE,{"disambiguationData":[TD([[makeQuery(id+"F14.imprint","IMPRINT",EDGE,{"derivedFrom":sQuery(id+"F14.wireOp",EDGE,"E75")}),-1.0]])]}),sQuery(id+"F15.wireOp",EDGE,"E85"),sQuery(id+"F16.wireOp",EDGE,"E95")])]});
            var Q1;
            Q1=qCreatedBy(makeId("Right.planeOp"),FACE);
            mirror(context, id + "F27", {"operationType" : NewBodyOperationType.ADD, "entities" : qUnion([Q0]), "mirrorPlane" : qUnion([Q1])});
        }
    });
